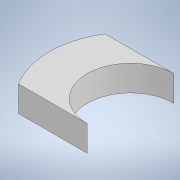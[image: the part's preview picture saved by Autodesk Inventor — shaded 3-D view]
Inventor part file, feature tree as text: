
AUTODESK INVENTOR PART (.ipt)
format: ipt  version: 2022.2 (Build 262287000, 287)  size: 99,328 bytes
history: native  units: mm
features: other x1, extrude x1, sketch x1
ambient origin geometry x8: Origin, YZ Plane, XZ Plane, XY Plane, X Axis, Y Axis, Z Axis, Center Point
bodies: Solid1 (feature_tree)
feature tree (3):
  other  "Crank.ipt"
  extrude  "Extrusion1"  Depth=10.0mm
  sketch  "Sketch1"  dims[d0=8.0mm d1=10.0mm d2=15.0mm d3=4.75mm d4=0.0mm]
